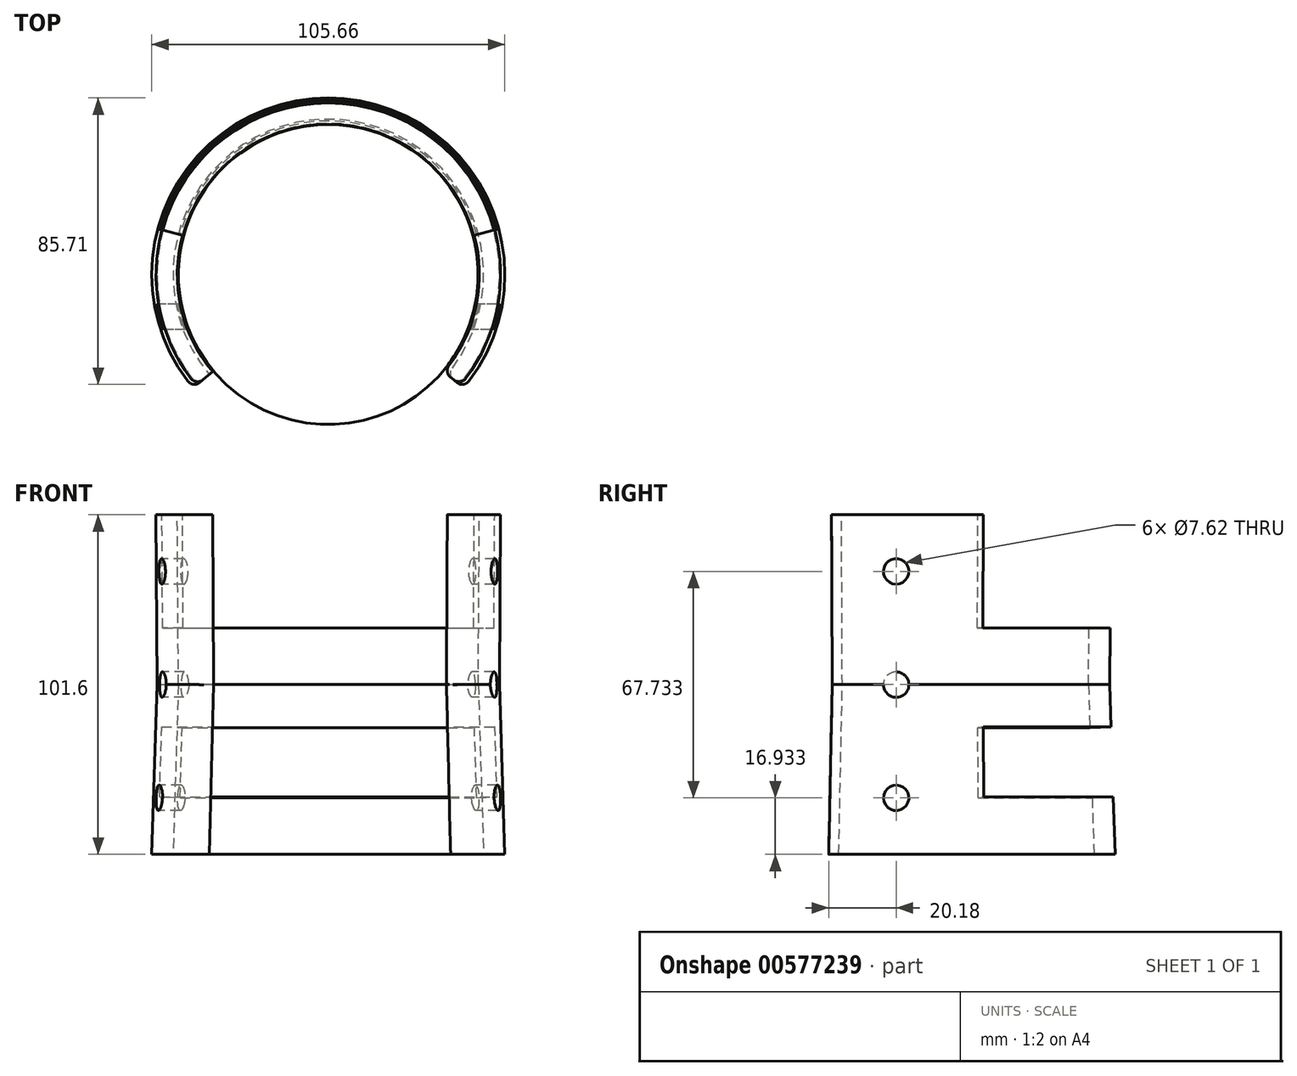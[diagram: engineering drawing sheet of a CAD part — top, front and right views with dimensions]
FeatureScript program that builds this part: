
annotation { "Feature Type Name" : "Feature", "Feature Type Description" : "" }
export const myFeature = defineFeature(function(context is Context, id is Id, definition is map)
    precondition{}
    {
        {
            var Q0;
            Q0=qCreatedBy(makeId("Front.planeOp"),FACE);
            var sketch = newSketch(context, id + "F0", { "sketchPlane" : qUnion([Q0])});
            skLineSegment(sketch, "E0", {"start": v(0, 0) * mm, "end": v(0, 50.8) * mm});
            skLineSegment(sketch, "E1", {"start": v(0, 0) * mm, "end": v(52.83, 0) * mm});
            skLineSegment(sketch, "E2", {"start": v(52.83, 0) * mm, "end": v(51.23, 50.8) * mm});
            skLineSegment(sketch, "E3", {"start": v(0, 50.8) * mm, "end": v(0, 101.6) * mm});
            skLineSegment(sketch, "E4", {"start": v(0, 101.6) * mm, "end": v(51.56, 101.6) * mm});
            skLineSegment(sketch, "E5", {"start": v(51.56, 101.6) * mm, "end": v(51.23, 50.8) * mm});
            skSolve(sketch);
        }
        {
            var Q0;
            Q0=qSketchRegion(id+"F0",true);
            var Q1;
            Q1=sQuery(id+"F0.wireOp",EDGE,"E3");
            revolve(context, id + "F1", {"entities" : qUnion([Q0]), "axis" : qUnion([Q1]), "revolveType" : RevolveType.SYMMETRIC, "angle" : 260 * degree});
        }
        {
            var Q0;
            Q0=qCreatedBy(makeId("Front.planeOp"),FACE);
            var sketch = newSketch(context, id + "F2", { "sketchPlane" : qUnion([Q0])});
            skLineSegment(sketch, "E6", {"start": v(0, 0) * mm, "end": v(0, 50.8) * mm});
            skLineSegment(sketch, "E7", {"start": v(0, 50.8) * mm, "end": v(0, 101.6) * mm});
            skLineSegment(sketch, "E8", {"start": v(0, 101.6) * mm, "end": v(45.21, 101.6) * mm});
            skLineSegment(sketch, "E9", {"start": v(0, 0) * mm, "end": v(46.48, 0) * mm});
            skLineSegment(sketch, "E10", {"start": v(0, 50.8) * mm, "end": v(44.88, 50.8) * mm, "construction": true});
            skLineSegment(sketch, "E11", {"start": v(44.88, 50.8) * mm, "end": v(45.21, 101.6) * mm});
            skLineSegment(sketch, "E12", {"start": v(44.88, 50.8) * mm, "end": v(46.48, 0) * mm});
            skSolve(sketch);
        }
        {
            var Q0;
            Q0=qSketchRegion(id+"F2",true);
            var Q1;
            Q1=sQuery(id+"F2.wireOp",EDGE,"E7");
            revolve(context, id + "F3", {"operationType" : NewBodyOperationType.REMOVE, "entities" : qUnion([Q0]), "axis" : qUnion([Q1]), "revolveType" : RevolveType.FULL, "oppositeDirection" : true});
        }
        {
            var Q0;
            Q0=makeQuery(id+"F3.boolean.opBoolean","INTERSECT",EDGE,{"disambiguationData":[OD(1.0)],"derivedFrom":[makeQuery(id+"F1.opRevolve","CAP_FACE",FACE,{"disambiguationData":[OSD([sQuery(id+"F0.wireOp",EDGE,"E0"),sQuery(id+"F0.wireOp",EDGE,"E1"),sQuery(id+"F0.wireOp",EDGE,"E2"),sQuery(id+"F0.wireOp",EDGE,"E3"),sQuery(id+"F0.wireOp",EDGE,"E4"),sQuery(id+"F0.wireOp",EDGE,"E5")])],"isStart":true}),makeQuery(id+"F3.opRevolve","SWEPT_FACE",FACE,{"disambiguationData":[OSD([sQuery(id+"F2.wireOp",EDGE,"E11")])]})]});
            var Q1;
            Q1=makeQuery(id+"F3.boolean.opBoolean","INTERSECT",EDGE,{"disambiguationData":[OD(0.0)],"derivedFrom":[makeQuery(id+"F1.opRevolve","CAP_FACE",FACE,{"disambiguationData":[OSD([sQuery(id+"F0.wireOp",EDGE,"E0"),sQuery(id+"F0.wireOp",EDGE,"E1"),sQuery(id+"F0.wireOp",EDGE,"E2"),sQuery(id+"F0.wireOp",EDGE,"E3"),sQuery(id+"F0.wireOp",EDGE,"E4"),sQuery(id+"F0.wireOp",EDGE,"E5")])],"isStart":true}),makeQuery(id+"F3.opRevolve","SWEPT_FACE",FACE,{"disambiguationData":[OSD([sQuery(id+"F2.wireOp",EDGE,"E11")])]})]});
            var Q2;
            Q2=makeQuery(id+"F1.opRevolve","CAP_EDGE",EDGE,{"disambiguationData":[OSD([sQuery(id+"F0.wireOp",EDGE,"E5")])],"isStart":true});
            var Q3;
            Q3=makeQuery(id+"F1.opRevolve","CAP_EDGE",EDGE,{"disambiguationData":[OSD([sQuery(id+"F0.wireOp",EDGE,"E5")])],"isStart":false});
            var Q4;
            Q4=makeQuery(id+"F3.boolean.opBoolean","INTERSECT",EDGE,{"disambiguationData":[OD(1.0)],"derivedFrom":[makeQuery(id+"F1.opRevolve","CAP_FACE",FACE,{"disambiguationData":[OSD([sQuery(id+"F0.wireOp",EDGE,"E0"),sQuery(id+"F0.wireOp",EDGE,"E1"),sQuery(id+"F0.wireOp",EDGE,"E2"),sQuery(id+"F0.wireOp",EDGE,"E3"),sQuery(id+"F0.wireOp",EDGE,"E4"),sQuery(id+"F0.wireOp",EDGE,"E5")])],"isStart":true}),makeQuery(id+"F3.opRevolve","SWEPT_FACE",FACE,{"disambiguationData":[OSD([sQuery(id+"F2.wireOp",EDGE,"E12")])]})]});
            var Q5;
            Q5=makeQuery(id+"F1.opRevolve","CAP_EDGE",EDGE,{"disambiguationData":[OSD([sQuery(id+"F0.wireOp",EDGE,"E2")])],"isStart":false});
            var Q6;
            Q6=makeQuery(id+"F3.boolean.opBoolean","INTERSECT",EDGE,{"disambiguationData":[OD(0.0)],"derivedFrom":[makeQuery(id+"F1.opRevolve","CAP_FACE",FACE,{"disambiguationData":[OSD([sQuery(id+"F0.wireOp",EDGE,"E0"),sQuery(id+"F0.wireOp",EDGE,"E1"),sQuery(id+"F0.wireOp",EDGE,"E2"),sQuery(id+"F0.wireOp",EDGE,"E3"),sQuery(id+"F0.wireOp",EDGE,"E4"),sQuery(id+"F0.wireOp",EDGE,"E5")])],"isStart":true}),makeQuery(id+"F3.opRevolve","SWEPT_FACE",FACE,{"disambiguationData":[OSD([sQuery(id+"F2.wireOp",EDGE,"E12")])]})]});
            var Q7;
            Q7=makeQuery(id+"F1.opRevolve","CAP_EDGE",EDGE,{"disambiguationData":[OSD([sQuery(id+"F0.wireOp",EDGE,"E2")])],"isStart":true});
            fillet(context, id + "F4", {"entities" : qUnion([Q0, Q1, Q2, Q3, Q4, Q5, Q6, Q7]), "radius" : 2.54 * mm, "tangentPropagation" : true, "allowEdgeOverflow" : false});
        }
        {
            var Q0;
            Q0=qCreatedBy(makeId("Front.planeOp"),FACE);
            var sketch = newSketch(context, id + "F5", { "sketchPlane" : qUnion([Q0])});
            skLineSegment(sketch, "E13", {"start": v(0, 0) * mm, "end": v(0, 50.8) * mm, "construction": true});
            skLineSegment(sketch, "E14", {"start": v(0, 50.8) * mm, "end": v(0, 101.6) * mm, "construction": true});
            skLineSegment(sketch, "E15", {"start": v(0, 101.6) * mm, "end": v(51.56, 101.6) * mm, "construction": true});
            skLineSegment(sketch, "E16", {"start": v(0, 0) * mm, "end": v(52.83, 0) * mm, "construction": true});
            skLineSegment(sketch, "E17", {"start": v(51.56, 101.6) * mm, "end": v(51.23, 50.8) * mm, "construction": true});
            skLineSegment(sketch, "E18", {"start": v(51.23, 50.8) * mm, "end": v(52.83, 0) * mm, "construction": true});
            skLineSegment(sketch, "E19", {"start": v(52.83, 0) * mm, "end": v(46.48, 0) * mm});
            skLineSegment(sketch, "E20", {"start": v(51.23, 50.8) * mm, "end": v(44.88, 50.8) * mm, "construction": true});
            skLineSegment(sketch, "E21", {"start": v(51.56, 101.6) * mm, "end": v(45.21, 101.6) * mm, "construction": true});
            skLineSegment(sketch, "E22", {"start": v(45.21, 101.6) * mm, "end": v(44.88, 50.8) * mm, "construction": true});
            skLineSegment(sketch, "E23", {"start": v(44.88, 50.8) * mm, "end": v(46.48, 0) * mm, "construction": true});
            skLineSegment(sketch, "E24", {"start": v(0, 0) * mm, "end": v(0, 16.93) * mm, "construction": true});
            skLineSegment(sketch, "E25", {"start": v(0, 16.93) * mm, "end": v(0, 33.87) * mm, "construction": true});
            skLineSegment(sketch, "E26", {"start": v(0, 50.8) * mm, "end": v(0, 67.73) * mm, "construction": true});
            skLineSegment(sketch, "E27", {"start": v(0, 67.73) * mm, "end": v(0, 84.67) * mm, "construction": true});
            skLineSegment(sketch, "E28", {"start": v(45.42, 33.66) * mm, "end": v(45.95, 16.93) * mm});
            skLineSegment(sketch, "E29", {"start": v(52.3, 17.13) * mm, "end": v(51.73, 35) * mm});
            skLineSegment(sketch, "E30", {"start": v(45, 67.73) * mm, "end": v(45.1, 84.37) * mm});
            skLineSegment(sketch, "E31", {"start": v(45, 67.73) * mm, "end": v(51.34, 67.7) * mm});
            skLineSegment(sketch, "E32", {"start": v(51.34, 67.7) * mm, "end": v(51.45, 84.37) * mm});
            skLineSegment(sketch, "E33", {"start": v(45.21, 101.6) * mm, "end": v(51.56, 101.6) * mm});
            skLineSegment(sketch, "E34", {"start": v(51.45, 84.37) * mm, "end": v(51.56, 101.6) * mm});
            skLineSegment(sketch, "E35", {"start": v(45.21, 101.6) * mm, "end": v(45.1, 84.37) * mm});
            skLineSegment(sketch, "E36", {"start": v(45.42, 33.66) * mm, "end": v(45.29, 37.89) * mm});
            skLineSegment(sketch, "E37", {"start": v(51.73, 35) * mm, "end": v(51.63, 38.17) * mm});
            skLineSegment(sketch, "E38", {"start": v(51.63, 38.17) * mm, "end": v(45.29, 37.89) * mm});
            skLineSegment(sketch, "E39", {"start": v(45.95, 16.93) * mm, "end": v(52.3, 17.13) * mm});
            skSolve(sketch);
        }
        {
            var Q0;
            Q0=qSketchRegion(id+"F5",true);
            var Q1;
            Q1=sQuery(id+"F2.wireOp",EDGE,"E7");
            revolve(context, id + "F6", {"operationType" : NewBodyOperationType.REMOVE, "entities" : qUnion([Q0]), "axis" : qUnion([Q1]), "revolveType" : RevolveType.SYMMETRIC, "angle" : 150 * degree});
        }
        {
            var Q0;
            Q0=qCreatedBy(makeId("Front.planeOp"),FACE);
            var sketch = newSketch(context, id + "F7", { "sketchPlane" : qUnion([Q0])});
            skLineSegment(sketch, "E40", {"start": v(0, 0) * mm, "end": v(0, 16.93) * mm, "construction": true});
            skLineSegment(sketch, "E41", {"start": v(0, 16.93) * mm, "end": v(0, 33.87) * mm, "construction": true});
            skLineSegment(sketch, "E42", {"start": v(0, 33.87) * mm, "end": v(0, 50.8) * mm, "construction": true});
            skLineSegment(sketch, "E43", {"start": v(0, 50.8) * mm, "end": v(0, 67.73) * mm, "construction": true});
            skLineSegment(sketch, "E44", {"start": v(0, 67.73) * mm, "end": v(0, 84.67) * mm, "construction": true});
            skLineSegment(sketch, "E45", {"start": v(0, 16.93) * mm, "end": v(-12.7, 16.93) * mm, "construction": true});
            skLineSegment(sketch, "E46", {"start": v(0, 50.8) * mm, "end": v(-12.7, 50.8) * mm, "construction": true});
            skLineSegment(sketch, "E47", {"start": v(0, 84.67) * mm, "end": v(-12.7, 84.67) * mm, "construction": true});
            skCircle(sketch, "E48", {"center": v(-12.7, 84.67) * mm, "radius": 3.81 * mm});
            skCircle(sketch, "E49", {"center": v(-12.7, 50.8) * mm, "radius": 3.81 * mm});
            skCircle(sketch, "E50", {"center": v(-12.7, 16.93) * mm, "radius": 3.81 * mm});
            skSolve(sketch);
        }
        {
            var Q0;
            Q0=qSketchRegion(id+"F7",true);
            extrude(context, id + "F8", {"entities" : qUnion([Q0]), "operationType" : NewBodyOperationType.REMOVE, "endBound" : BoundingType.SYMMETRIC, "depth" : 127 * mm, "offsetDistance" : 25.4 * mm});
        }
        {
            var Q0;
            Q0=makeQuery(id+"F1.opRevolve","SWEPT_BODY",BODY,{"disambiguationData":[OSD([sQuery(id+"F0.wireOp",EDGE,"E0"),sQuery(id+"F0.wireOp",EDGE,"E1"),sQuery(id+"F0.wireOp",EDGE,"E2"),sQuery(id+"F0.wireOp",EDGE,"E3"),sQuery(id+"F0.wireOp",EDGE,"E4"),sQuery(id+"F0.wireOp",EDGE,"E5")])]});
            var Q1;
            Q1=sQuery(id+"F2.wireOp",EDGE,"E7");
            transform(context, id + "F9", {"entities" : qUnion([Q0]), "transformType" : TransformType.ROTATION, "transformAxis" : qUnion([Q1]), "angle" : 90 * degree, "makeCopy" : false});
        }
    });
